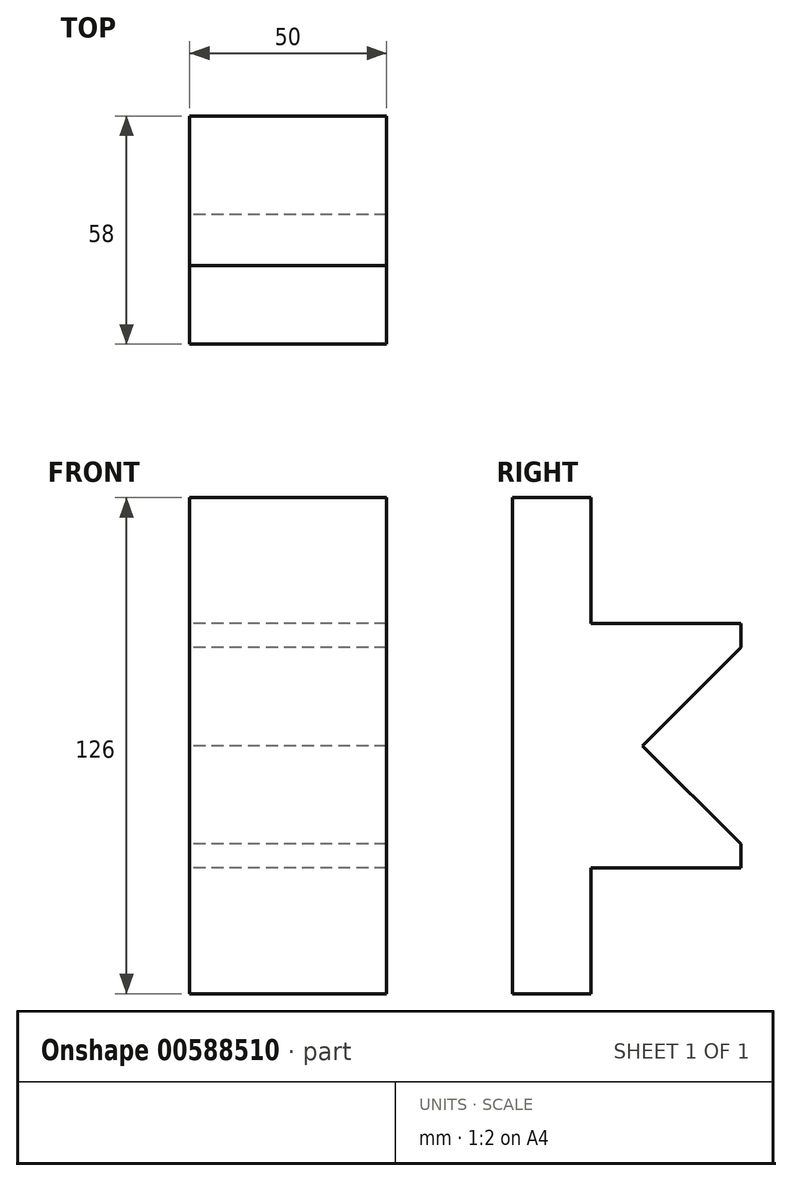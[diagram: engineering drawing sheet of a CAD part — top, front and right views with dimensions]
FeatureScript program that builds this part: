
annotation { "Feature Type Name" : "Feature", "Feature Type Description" : "" }
export const myFeature = defineFeature(function(context is Context, id is Id, definition is map)
    precondition{}
    {
        {
            var Q0;
            Q0=qCreatedBy(makeId("Right.planeOp"),FACE);
            var sketch = newSketch(context, id + "F0", { "sketchPlane" : qUnion([Q0])});
            skLineSegment(sketch, "E0", {"start": v(0, 0) * mm, "end": v(0, -63) * mm});
            skLineSegment(sketch, "E1", {"start": v(0, -63) * mm, "end": v(20, -63) * mm});
            skLineSegment(sketch, "E2", {"start": v(20, -63) * mm, "end": v(20, -31) * mm});
            skLineSegment(sketch, "E3", {"start": v(20, -31) * mm, "end": v(58, -31) * mm});
            skLineSegment(sketch, "E4", {"start": v(58, -31) * mm, "end": v(58, -25) * mm});
            skLineSegment(sketch, "E5", {"start": v(58, -25) * mm, "end": v(33, 0) * mm});
            skLineSegment(sketch, "E6", {"start": v(33, 0) * mm, "end": v(58, 25) * mm});
            skLineSegment(sketch, "E7", {"start": v(58, 25) * mm, "end": v(58, 31) * mm});
            skLineSegment(sketch, "E8", {"start": v(58, 31) * mm, "end": v(20, 31) * mm});
            skLineSegment(sketch, "E9", {"start": v(20, 31) * mm, "end": v(20, 63) * mm});
            skLineSegment(sketch, "E10", {"start": v(20, 63) * mm, "end": v(0, 63) * mm});
            skLineSegment(sketch, "E11", {"start": v(0, 63) * mm, "end": v(0, 0) * mm});
            skSolve(sketch);
        }
        {
            var Q0;
            Q0=makeQuery(id+"F0.imprint","IMPRINT",FACE,{"disambiguationData":[TD([[makeQuery(id+"F0.imprint","IMPRINT",EDGE,{"derivedFrom":sQuery(id+"F0.wireOp",EDGE,"E0")}),1.0]])]});
            extrude(context, id + "F1", {"entities" : qUnion([Q0]), "depth" : 50 * mm, "offsetDistance" : 25 * mm});
        }
    });
